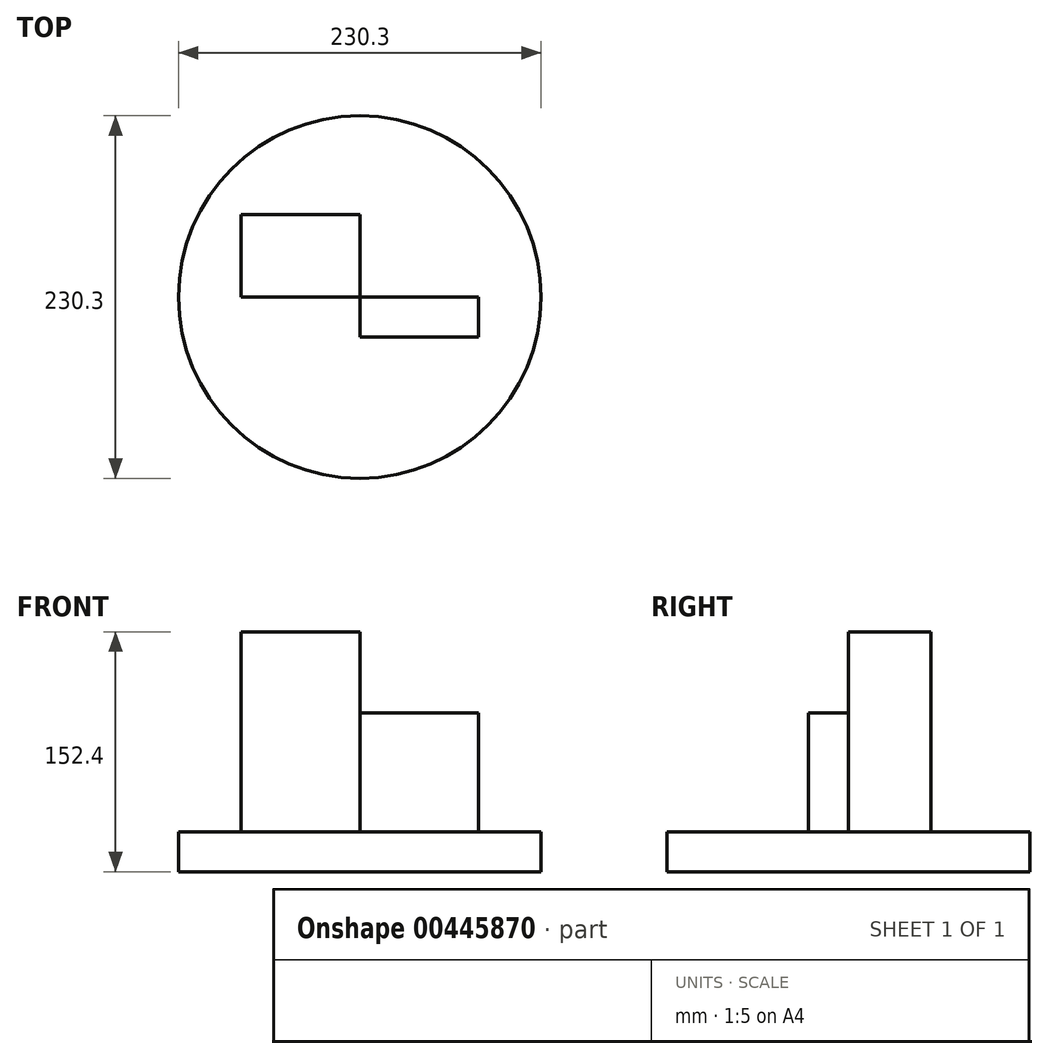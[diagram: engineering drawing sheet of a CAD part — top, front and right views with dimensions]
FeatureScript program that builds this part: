
annotation { "Feature Type Name" : "Feature", "Feature Type Description" : "" }
export const myFeature = defineFeature(function(context is Context, id is Id, definition is map)
    precondition{}
    {
        {
            var Q0;
            Q0=qCreatedBy(makeId("Front.planeOp"),FACE);
            var sketch = newSketch(context, id + "F0", { "sketchPlane" : qUnion([Q0])});
            skLineSegment(sketch, "E0.bottom", {"start": v(0, 0) * mm, "end": v(75.42, 0) * mm});
            skLineSegment(sketch, "E0.top", {"start": v(0, 75.38) * mm, "end": v(75.42, 75.38) * mm});
            skLineSegment(sketch, "E0.left", {"start": v(0, 0) * mm, "end": v(0, 75.38) * mm});
            skLineSegment(sketch, "E0.right", {"start": v(75.42, 0) * mm, "end": v(75.42, 75.38) * mm});
            skSolve(sketch);
        }
        {
            var Q0;
            Q0 = qSketchRegion(id + "F0", true);
            extrude(context, id + "F1", {"entities" : qUnion([Q0]), "depth" : 25.4 * mm});
        }
        {
            var Q0;
            Q0=qCreatedBy(makeId("Top.planeOp"),FACE);
            var sketch = newSketch(context, id + "F2", { "sketchPlane" : qUnion([Q0])});
            skLineSegment(sketch, "E1.bottom", {"start": v(0, 0) * mm, "end": v(-75.44, 0) * mm});
            skLineSegment(sketch, "E1.top", {"start": v(0, 52.45) * mm, "end": v(-75.44, 52.45) * mm});
            skLineSegment(sketch, "E1.left", {"start": v(0, 0) * mm, "end": v(0, 52.45) * mm});
            skLineSegment(sketch, "E1.right", {"start": v(-75.44, 0) * mm, "end": v(-75.44, 52.45) * mm});
            skSolve(sketch);
        }
        {
            var Q0;
            Q0 = qSketchRegion(id + "F2", true);
            extrude(context, id + "F3", {"entities" : qUnion([Q0]), "depth" : 127 * mm});
        }
        {
            var Q0;
            Q0=qCreatedBy(makeId("Top.planeOp"),FACE);
            var sketch = newSketch(context, id + "F4", { "sketchPlane" : qUnion([Q0])});
            skCircle(sketch, "E2", {"center": v(0, 0) * mm, "radius": 115.15 * mm});
            skSolve(sketch);
        }
        {
            var Q0;
            Q0 = qSketchRegion(id + "F4", true);
            extrude(context, id + "F5", {"entities" : qUnion([Q0]), "oppositeDirection" : true, "depth" : 25.4 * mm});
        }
    });
